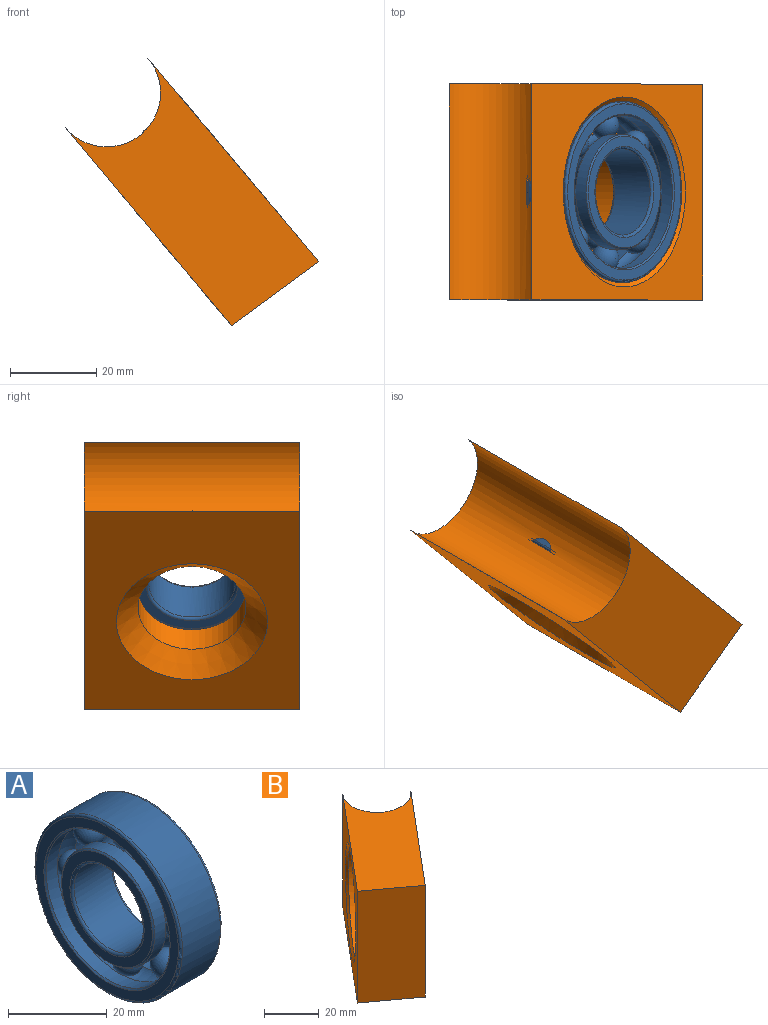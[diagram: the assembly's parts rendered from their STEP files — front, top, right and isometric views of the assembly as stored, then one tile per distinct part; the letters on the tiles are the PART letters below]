
ASSEMBLY  parts=2 mates=1
PART A: 42 faces, bbox 12x45.5x45.5 mm
  f0: plane 40.8x40.8mm, normal (-1,0,0), area 283.9mm2, adj f1,f18
  f1: torus R=20.4mm, axis (1,0,0), area 123.1mm2, adj f0,f2
  f2: cylinder r=21mm len=42mm, axis (1,0,0), area 1425mm2, adj f1,f3
  f3: torus R=20.4mm, axis (1,0,0), area 123.1mm2, adj f2,f4
  f4: plane 40.8x40.8mm, normal (1,0,0), area 283.9mm2, adj f3,f5
  f5: cone r=17.87mm half-angle=45deg, axis (1,0,0), area 55.5mm2, adj f4,f6
  f6: cylinder r=17.7mm len=35.4mm, axis (1,0,0), area 354.8mm2, adj f5,f7,f8,f9,f10,f11,f12,f13
  f7: sphere r=3.32mm, area 130.9mm2, adj f6,f11,f12,f17,f19,f27,f31,f32
  f8: torus R=15.5mm, axis (1,0,0), area 76.3mm2, adj f6,f16,f17,f36
  f9: torus R=15.5mm, axis (1,0,0), area 76.3mm2, adj f6,f16,f17,f38
  f10: torus R=15.5mm, axis (1,0,0), area 76.3mm2, adj f6,f17,f37,f38
  f11: torus R=15.5mm, axis (1,0,0), area 76.3mm2, adj f6,f7,f17,f37
  f12: torus R=15.5mm, axis (1,0,0), area 76.3mm2, adj f6,f7,f17,f39
  f13: torus R=15.5mm, axis (1,0,0), area 76.3mm2, adj f6,f17,f39,f40
  f14: torus R=15.5mm, axis (1,0,0), area 76.3mm2, adj f6,f17,f40,f41
  f15: torus R=15.5mm, axis (1,0,0), area 76.3mm2, adj f6,f17,f36,f41
  f16: sphere r=3.32mm, area 130.9mm2, adj f6,f8,f9,f17,f19,f27,f28,f29
  f17: cylinder r=17.7mm len=35.4mm, axis (1,0,0), area 354.8mm2, adj f7,f8,f9,f10,f11,f12,f13,f14
  f18: cone r=17.87mm half-angle=45deg, axis (-1,0,0), area 55.5mm2, adj f0,f17
  f19: cylinder r=13.3mm len=26.6mm, axis (1,0,0), area 266.6mm2, adj f7,f16,f20,f28,f29,f30,f31,f32
  f20: cone r=13.13mm half-angle=45deg, axis (1,0,0), area 40.8mm2, adj f19,f21
  f21: plane 25.9x25.9mm, normal (-1,0,0), area 173.9mm2, adj f20,f22
  f22: torus R=10.6mm, axis (1,0,0), area 60.5mm2, adj f21,f23
  f23: cylinder r=10mm len=20mm, axis (1,0,0), area 678.6mm2, adj f22,f24
  f24: torus R=10.6mm, axis (1,0,0), area 60.5mm2, adj f23,f25
  f25: plane 25.9x25.9mm, normal (1,0,0), area 173.9mm2, adj f24,f26
  f26: cone r=13.13mm half-angle=45deg, axis (-1,0,0), area 40.8mm2, adj f25,f27
  f27: cylinder r=13.3mm len=26.6mm, axis (1,0,0), area 266.6mm2, adj f7,f16,f26,f28,f29,f30,f31,f32
  f28: torus R=15.5mm, axis (1,0,0), area 51.5mm2, adj f16,f19,f27,f36
  f29: torus R=15.5mm, axis (1,0,0), area 51.5mm2, adj f16,f19,f27,f38
  f30: torus R=15.5mm, axis (1,0,0), area 51.5mm2, adj f19,f27,f37,f38
  f31: torus R=15.5mm, axis (1,0,0), area 51.5mm2, adj f7,f19,f27,f37
  f32: torus R=15.5mm, axis (1,0,0), area 51.5mm2, adj f7,f19,f27,f39
  f33: torus R=15.5mm, axis (1,0,0), area 51.5mm2, adj f19,f27,f39,f40
  f34: torus R=15.5mm, axis (1,0,0), area 51.5mm2, adj f19,f27,f40,f41
  f35: torus R=15.5mm, axis (1,0,0), area 51.5mm2, adj f19,f27,f36,f41
  f36: sphere r=3.32mm, area 130.9mm2, adj f6,f8,f15,f17,f19,f27,f28,f35
  f37: sphere r=3.32mm, area 130.9mm2, adj f6,f10,f11,f17,f19,f27,f30,f31
  f38: sphere r=3.32mm, area 130.9mm2, adj f6,f9,f10,f17,f19,f27,f29,f30
  f39: sphere r=3.32mm, area 130.9mm2, adj f6,f12,f13,f17,f19,f27,f32,f33
  f40: sphere r=3.32mm, area 130.9mm2, adj f6,f13,f14,f17,f19,f27,f33,f34
  f41: sphere r=3.32mm, area 130.9mm2, adj f6,f14,f15,f17,f19,f27,f34,f35
PART B: 12 faces, bbox 58.7x62x50 mm
  f0: plane 50x47.12mm, normal (-0.77,0.64,0), area 1555.2mm2, adj f1,f3,f4,f5,f10
  f1: plane 50x20.19mm, normal (-0.59,-0.81,0), area 1252.6mm2, adj f0,f2,f4,f5
  f2: plane 50x45.89mm, normal (0.77,-0.64,0), area 2032.9mm2, adj f1,f3,f4,f5,f11
  f3: cylinder r=12.5mm len=50mm, axis (0,0,-1), area 1955.2mm2, adj f0,f2,f4,f5,f7,f8
  f4: plane 61.96x58.69mm, normal (0,0,1), area 1272.3mm2, adj f0,f1,f2,f3
  f5: plane 61.96x58.69mm, normal (0,0,-1), area 1272.3mm2, adj f0,f1,f2,f3
  f6: cylinder r=12.5mm len=25mm, axis (0.77,-0.64,0), area 549.8mm2, adj f9,f11
  f7: cylinder r=21mm len=42mm, axis (-0.77,0.64,0), area 1443.1mm2, adj f3,f8,f10
  f8: plane 42x32.01mm, normal (-0.77,0.64,0), area 812mm2, adj f3,f7,f9
  f9: cone r=12.5mm half-angle=45deg, axis (-0.77,0.64,0), area 115.5mm2, adj f6,f8
  f10: cone r=21mm half-angle=45deg, axis (-0.77,0.64,0), area 191mm2, adj f0,f7
  f11: cone r=12.5mm half-angle=45deg, axis (0.77,-0.64,0), area 666.4mm2, adj f2,f6
PLACE A rot(axis=(0,-1,0),40deg) t=(-138.19,0.09,-22)mm
PLACE B rot(axis=(0,0.71,0.71),180deg) t=(0.89,0.09,-0.68)mm
MATE fastened A.f1 <-> B.f7  axis (-0.77,0,-0.64) through (-142.79,0.09,-25.85)mm
